# Revit family: Plumbing-Fix_Soap-Disp-Touchless_Stern_Extreme-Plus
name_source: partatom
category: Plumbing Fixtures
units: mm (PartAtom-declared; Revit-internal decimal feet)

## family parameters
Classification Number = 23.45.05.00
Cut with Voids When Loaded = No
Enable Cutting in Views = No
Host = Face
Maintain Annotation Orientation = No
Part Type = Normal
Room Calculation Point = No
Round Connector Dimension = Use Diameter
Shared = No

## types (12) — shared parameters
Assembly Code = D2010300
Available Options = as Specified
CW Connection = No
Default Elevation = 0' - 0"
HW Connection = No
Link to Related Files = https://www.arcat.com
Manufacturer = Stern Engineering
Manufacturer Website = http://www.sternfaucets.com
Product Data = http://www.arcat.com
Product Features = as Specified
Revision = R1_2018-04
Sales Information = http://www.sternfaucets.com
Spout Reach = 0' - 3 1/2"
Standards Conformance = as Specified
Type Comments = as Specified
URL = http://www.sternfaucets.com
Unit Width = 0' - 1 1/2"
Vent Connection = No
Warranty Duration (Years) = 2
Waste Connection = No
zero-valued in all types: CWFU, Cost, Expected Lifespan (Years), HWFU, Maintenance Schedule (Months), WFU

## per-type parameters (varying)
| type | Capacity | Description | Extension Option Selection | Include MF Pump | Model | Power Supply |
| Standard Battery Pack | 33 oz / 1 liter Liquid | Stern Touchless Deck Mounted Soap Dispenser - Extreme Soap Dispenser Plus B as Specified | 1 | No | Extreme Soap Dispenser Plus B | 6x DD Batteries |
| Standard Transformer | 33 oz / 1 liter Liquid | Stern Touchless Deck Mounted Soap Dispenser - Extreme Soap Dispenser Plus E as Specified | 1 | No | Extreme Soap Dispenser Plus E | 12V Transformer |
| Multifeed Liquid | as Specified | Stern Touchless Deck Mounted Soap Dispenser - MF Extreme Soap Dispenser Plus as Specified | 1 | Yes | MF Extreme Soap Dispenser Plus | 12V Transformer |
| Standard Battery Pack w/ 93mm Extension | 33 oz / 1 liter Liquid | Stern Touchless Deck Mounted Soap Dispenser - Extreme Soap Dispenser Plus B as Specified | 2 | No | Extreme Soap Dispenser Plus B | 6x DD Batteries |
| Standard Transformer w/ 93mm Extension | 33 oz / 1 liter Liquid | Stern Touchless Deck Mounted Soap Dispenser - Extreme Soap Dispenser Plus E as Specified | 2 | No | Extreme Soap Dispenser Plus E | 12V Transformer |
| Multifeed Liquid w/ 93mm Extension | as Specified | Stern Touchless Deck Mounted Soap Dispenser - MF Extreme Soap Dispenser Plus as Specified | 2 | Yes | MF Extreme Soap Dispenser Plus | 12V Transformer |
| Standard Battery Pack w/ 100mm Extension | 33 oz / 1 liter Liquid | Stern Touchless Deck Mounted Soap Dispenser - Extreme Soap Dispenser Plus B as Specified | 3 | No | Extreme Soap Dispenser Plus B | 6x DD Batteries |
| Standard Transformer w/ 100mm Extension | 33 oz / 1 liter Liquid | Stern Touchless Deck Mounted Soap Dispenser - Extreme Soap Dispenser Plus E as Specified | 3 | No | Extreme Soap Dispenser Plus E | 12V Transformer |
| Multifeed Liquid w/ 100mm Extension | as Specified | Stern Touchless Deck Mounted Soap Dispenser - MF Extreme Soap Dispenser Plus as Specified | 3 | Yes | MF Extreme Soap Dispenser Plus | 12V Transformer |
| Standard Battery Pack w/ 230mm Extension | 33 oz / 1 liter Liquid | Stern Touchless Deck Mounted Soap Dispenser - Extreme Soap Dispenser Plus B as Specified | 4 | No | Extreme Soap Dispenser Plus B | 6x DD Batteries |
| Standard Transformer w/ 230mm Extension | 33 oz / 1 liter Liquid | Stern Touchless Deck Mounted Soap Dispenser - Extreme Soap Dispenser Plus E as Specified | 4 | No | Extreme Soap Dispenser Plus E | 12V Transformer |
| Multifeed Liquid w/ 230mm Extension | as Specified | Stern Touchless Deck Mounted Soap Dispenser - MF Extreme Soap Dispenser Plus as Specified | 4 | Yes | MF Extreme Soap Dispenser Plus | 12V Transformer |

## geometry (parser evidence)
native form markers: Sweep x4
no freeform markers — native parametric forms only
